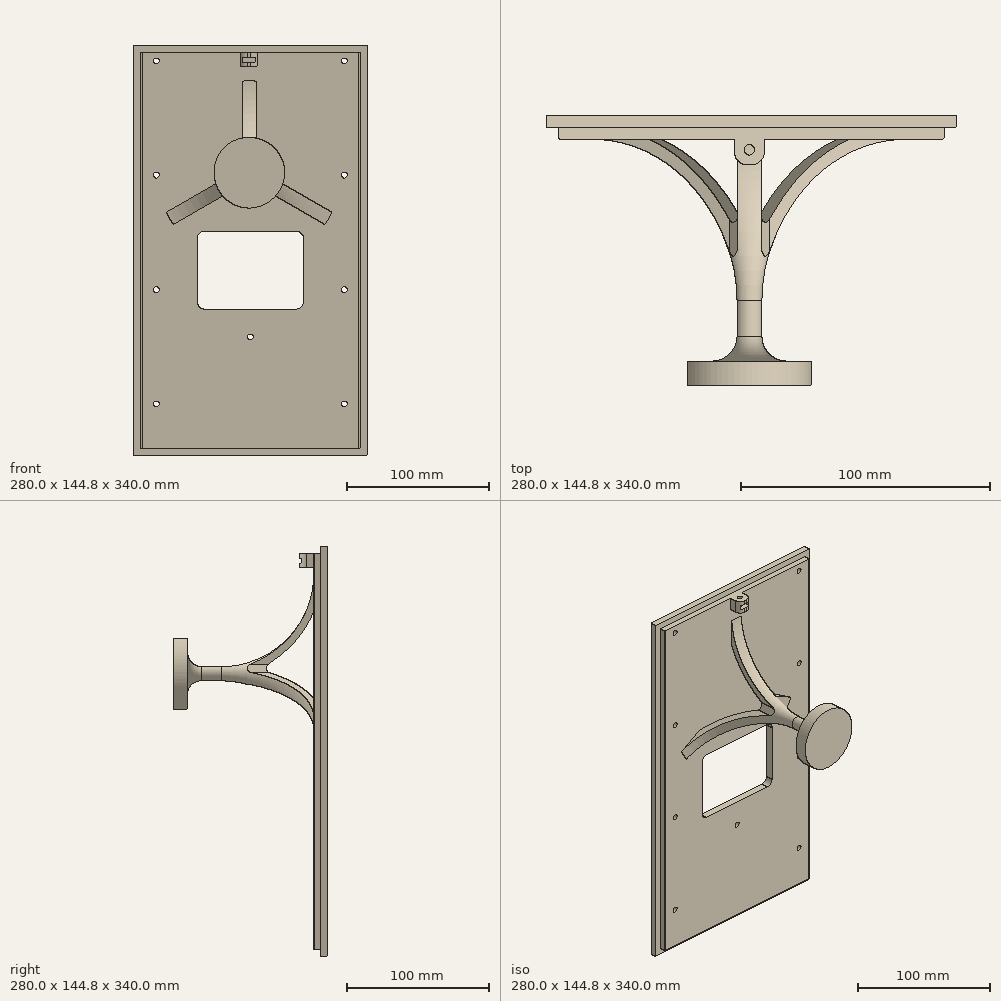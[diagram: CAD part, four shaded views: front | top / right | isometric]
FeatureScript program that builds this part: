
annotation { "Feature Type Name" : "Feature", "Feature Type Description" : "" }
export const myFeature = defineFeature(function(context is Context, id is Id, definition is map)
    precondition{}
    {
        {
            var Q0;
            Q0=qCreatedBy(makeId("Top.planeOp"),FACE);
            var sketch = newSketch(context, id + "F0", { "sketchPlane" : qUnion([Q0])});
            skLineSegment(sketch, "E0.bottom", {"start": v(-71.69, -76.13) * mm, "end": v(73.31, -76.13) * mm});
            skLineSegment(sketch, "E0.top", {"start": v(-71.69, 73.87) * mm, "end": v(73.31, 73.87) * mm});
            skLineSegment(sketch, "E0.left", {"start": v(-71.69, -76.13) * mm, "end": v(-71.69, 73.87) * mm});
            skLineSegment(sketch, "E0.right", {"start": v(73.31, -76.13) * mm, "end": v(73.31, 73.87) * mm});
            skPoint(sketch, "E0.middle", {"position": v(0.81, -1.13) * mm});
            skLineSegment(sketch, "E1.bottom", {"start": v(-81.69, -86.13) * mm, "end": v(83.31, -86.13) * mm});
            skLineSegment(sketch, "E1.top", {"start": v(-81.69, 83.87) * mm, "end": v(83.31, 83.87) * mm});
            skLineSegment(sketch, "E1.left", {"start": v(-81.69, -86.13) * mm, "end": v(-81.69, 83.87) * mm});
            skLineSegment(sketch, "E1.right", {"start": v(83.31, -86.13) * mm, "end": v(83.31, 83.87) * mm});
            skLineSegment(sketch, "E2", {"start": v(83.31, -81.13) * mm, "end": v(78.31, -81.13) * mm});
            skLineSegment(sketch, "E3", {"start": v(78.31, -81.13) * mm, "end": v(78.31, -76.13) * mm});
            skLineSegment(sketch, "E4", {"start": v(78.31, -76.13) * mm, "end": v(73.31, -76.13) * mm});
            skLineSegment(sketch, "E5", {"start": v(0.81, -86.13) * mm, "end": v(0.81, 83.87) * mm, "construction": true});
            skLineSegment(sketch, "E6", {"start": v(-81.69, -1.13) * mm, "end": v(83.31, -1.13) * mm, "construction": true});
            skLineSegment(sketch, "E7.MirrorCS", {"start": v(-76.69, -76.13) * mm, "end": v(-71.69, -76.13) * mm});
            skLineSegment(sketch, "E8.MirrorCS", {"start": v(-76.69, -81.13) * mm, "end": v(-76.69, -76.13) * mm});
            skLineSegment(sketch, "E9.MirrorCS", {"start": v(-81.69, -81.13) * mm, "end": v(-76.69, -81.13) * mm});
            skLineSegment(sketch, "E10.MirrorCS", {"start": v(83.31, 78.87) * mm, "end": v(78.31, 78.87) * mm});
            skLineSegment(sketch, "E11.MirrorCS", {"start": v(78.31, 78.87) * mm, "end": v(78.31, 73.87) * mm});
            skLineSegment(sketch, "E12.MirrorCS", {"start": v(78.31, 73.87) * mm, "end": v(73.31, 73.87) * mm});
            skLineSegment(sketch, "E13.MirrorCS", {"start": v(-76.69, 73.87) * mm, "end": v(-71.69, 73.87) * mm});
            skLineSegment(sketch, "E14.MirrorCS", {"start": v(-76.69, 78.87) * mm, "end": v(-76.69, 73.87) * mm});
            skLineSegment(sketch, "E15.MirrorCS", {"start": v(-81.69, 78.87) * mm, "end": v(-76.69, 78.87) * mm});
            skSolve(sketch);
        }
        {
            var Q0;
            Q0=makeQuery(id+"F0.imprint","IMPRINT",FACE,{"disambiguationData":[TD([[makeQuery(id+"F0.imprint","IMPRINT",EDGE,{"derivedFrom":sQuery(id+"F0.wireOp",EDGE,"E0.top")}),1.0]])]});
            extrude(context, id + "F1", {"entities" : qUnion([Q0]), "depth" : 290 * mm});
        }
        {
            var Q0;
            Q0=makeQuery(id+"F1.opExtrude","SWEPT_FACE",FACE,{"disambiguationData":[OSD([sQuery(id+"F0.wireOp",EDGE,"E11.MirrorCS")])]});
            var sketch = newSketch(context, id + "F2", { "sketchPlane" : qUnion([Q0])});
            skLineSegment(sketch, "E16.bottom", {"start": v(73.87, 290) * mm, "end": v(78.87, 290) * mm});
            skLineSegment(sketch, "E16.top", {"start": v(73.87, 285) * mm, "end": v(78.87, 285) * mm});
            skLineSegment(sketch, "E16.left", {"start": v(73.87, 290) * mm, "end": v(73.87, 285) * mm});
            skLineSegment(sketch, "E16.right", {"start": v(78.87, 290) * mm, "end": v(78.87, 285) * mm});
            skLineSegment(sketch, "E17.bottom", {"start": v(73.87, 0) * mm, "end": v(78.87, 0) * mm});
            skLineSegment(sketch, "E17.top", {"start": v(73.87, 5) * mm, "end": v(78.87, 5) * mm});
            skLineSegment(sketch, "E17.left", {"start": v(73.87, 0) * mm, "end": v(73.87, 5) * mm});
            skLineSegment(sketch, "E17.right", {"start": v(78.87, 0) * mm, "end": v(78.87, 5) * mm});
            skSolve(sketch);
        }
        {
            var Q0;
            Q0 = qSketchRegion(id + "F2", true);
            extrude(context, id + "F3", {"entities" : qUnion([Q0]), "operationType" : NewBodyOperationType.REMOVE, "endBound" : BoundingType.THROUGH_ALL, "oppositeDirection" : true, "depth" : 25 * mm});
        }
        {
            var Q0;
            Q0=makeQuery(id+"F1.opExtrude","SWEPT_FACE",FACE,{"disambiguationData":[OSD([sQuery(id+"F0.wireOp",EDGE,"E0.top"),sQuery(id+"F0.wireOp",EDGE,"E12.MirrorCS"),sQuery(id+"F0.wireOp",EDGE,"E13.MirrorCS")])]});
            var sketch = newSketch(context, id + "F4", { "sketchPlane" : qUnion([Q0])});
            skLineSegment(sketch, "E18", {"start": v(0, 290.68) * mm, "end": v(0, 0) * mm, "construction": true});
            skSolve(sketch);
        }
        {
            var Q0;
            Q0=sQuery(id+"F4.wireOp",EDGE,"A8UNbsVJ-gzvh-xwWj-zYQc-NNIxl5t48NZl");
            var Q1;
            Q1=sQuery(id+"F4.wireOp",EDGE,"E18");
            cPlane(context, id + "F5", {"entities" : qUnion([Q0, Q1]), "cplaneType" : CPlaneType.LINE_ANGLE, "offset" : 25 * mm, "angle" : 0 * degree, "width" : 150 * mm, "height" : 150 * mm});
        }
        {
            var Q0;
            Q0=qCreatedBy(id+"F5.planeOp",FACE);
            var sketch = newSketch(context, id + "F6", { "sketchPlane" : qUnion([Q0])});
            skLineSegment(sketch, "E19", {"start": v(15.13, 205) * mm, "end": v(15.13, 225) * mm});
            skLineSegment(sketch, "E20", {"start": v(15.13, 225) * mm, "end": v(25.13, 225) * mm});
            skLineSegment(sketch, "E21", {"start": v(25.13, 225) * mm, "end": v(25.13, 200) * mm});
            skLineSegment(sketch, "E22", {"start": v(25.13, 200) * mm, "end": v(-9.07, 200) * mm});
            skLineSegment(sketch, "E23", {"start": v(15.13, 205) * mm, "end": v(-9.07, 205) * mm});
            skPoint(sketch, "E24.visualSharp", {"position": v(-73.87, 205) * mm});
            skArc(sketch, "E24.filletArc", {"start": v(-73.87, 265) * mm, "mid": v(-53.22, 222.3) * mm, "end": v(-9.07, 205) * mm});
            skLineSegment(sketch, "E25", {"start": v(-73.87, 265) * mm, "end": v(-73.87, 243.54) * mm});
            skArc(sketch, "E26.0", {"start": v(-73.87, 243.54) * mm, "mid": v(-48.1, 211.9) * mm, "end": v(-9.07, 200) * mm});
            skSolve(sketch);
        }
        {
            var Q0;
            Q0=makeQuery(id+"F6.imprint","IMPRINT",FACE,{"disambiguationData":[TD([[makeQuery(id+"F6.imprint","IMPRINT",EDGE,{"derivedFrom":sQuery(id+"F6.wireOp",EDGE,"E19")}),-1.0]])]});
            var Q1;
            Q1=sQuery(id+"F6.wireOp",EDGE,"E22");
            revolve(context, id + "F7", {"operationType" : NewBodyOperationType.ADD, "entities" : qUnion([Q0]), "axis" : qUnion([Q1]), "revolveType" : RevolveType.FULL});
        }
        {
            var Q0;
            {var subQ0=sQuery(id+"F0.wireOp",EDGE,"E12.MirrorCS");var subQ1=sQuery(id+"F0.wireOp",EDGE,"E11.MirrorCS");Q0=makeQuery(id+"F4.imprint","IMPRINT",FACE,{"disambiguationData":[TD([[makeQuery(id+"F4.imprint","IMPRINT",EDGE,{"derivedFrom":makeQuery(id+"F1.opExtrude","SWEPT_EDGE",EDGE,{"disambiguationData":[OSD([subQ1,subQ0])]})}),-1.0]])]});}
            var sketch = newSketch(context, id + "F8", { "sketchPlane" : qUnion([Q0])});
            skLineSegment(sketch, "E27", {"start": v(0, 200) * mm, "end": v(0, 275.12) * mm, "construction": true});
            skLineSegment(sketch, "E28.left", {"start": v(5, 206.37) * mm, "end": v(5, 268.75) * mm});
            skLineSegment(sketch, "E28.right", {"start": v(-5, 206.37) * mm, "end": v(-5, 268.75) * mm});
            skPoint(sketch, "E28.middle", {"position": v(0, 237.56) * mm});
            skLineSegment(sketch, "E29.1.0", {"start": v(-8.02, 201.15) * mm, "end": v(-62.04, 169.95) * mm});
            skLineSegment(sketch, "E29.1.1", {"start": v(0, 200) * mm, "end": v(-65.06, 162.44) * mm, "construction": true});
            skLineSegment(sketch, "E29.1.2", {"start": v(-3.02, 192.49) * mm, "end": v(-57.04, 161.3) * mm});
            skLineSegment(sketch, "E29.2.0", {"start": v(3.02, 192.49) * mm, "end": v(57.04, 161.3) * mm});
            skLineSegment(sketch, "E29.2.1", {"start": v(0, 200) * mm, "end": v(65.06, 162.44) * mm, "construction": true});
            skLineSegment(sketch, "E29.2.2", {"start": v(8.02, 201.15) * mm, "end": v(62.04, 169.95) * mm});
            skPoint(sketch, "E29.center", {"position": v(0, 200) * mm});
            skArc(sketch, "E30", {"start": v(-57.04, 161.3) * mm, "mid": v(0, 131.07) * mm, "end": v(57.04, 161.3) * mm});
            skArc(sketch, "E31.trimOffspring", {"start": v(62.04, 169.95) * mm, "mid": v(59.7, 234.47) * mm, "end": v(5, 268.75) * mm});
            skArc(sketch, "E32.trimOffspring", {"start": v(-5, 268.75) * mm, "mid": v(-59.7, 234.47) * mm, "end": v(-62.04, 169.95) * mm});
            skLineSegment(sketch, "E33", {"start": v(-5, 206.37) * mm, "end": v(-8.02, 201.15) * mm});
            skLineSegment(sketch, "E34", {"start": v(-3.02, 192.49) * mm, "end": v(3.02, 192.49) * mm});
            skLineSegment(sketch, "E35", {"start": v(8.02, 201.15) * mm, "end": v(5, 206.37) * mm});
            skSolve(sketch);
        }
        {
            var Q0;
            Q0 = qSketchRegion(id + "F8", true);
            var Q1;
            Q1=makeQuery(id+"F7.opRevolve","SWEPT_FACE",FACE,{"disambiguationData":[OSD([sQuery(id+"F6.wireOp",EDGE,"E19")])]});
            extrude(context, id + "F9", {"entities" : qUnion([Q0]), "operationType" : NewBodyOperationType.REMOVE, "endBound" : BoundingType.UP_TO_SURFACE, "endBoundEntityFace" : qUnion([Q1]), "depth" : 25 * mm});
        }
        {
            var Q0;
            Q0=makeQuery(id+"F1.opExtrude","SWEPT_FACE",FACE,{"disambiguationData":[OSD([sQuery(id+"F0.wireOp",EDGE,"E1.top")])]});
            var sketch = newSketch(context, id + "F10", { "sketchPlane" : qUnion([Q0])});
            skPoint(sketch, "E36", {"position": v(-67.31, 279) * mm});
            skPoint(sketch, "E37.0.1.0", {"position": v(-67.31, 198.17) * mm});
            skPoint(sketch, "E37.0.2.0", {"position": v(-67.31, 117.33) * mm});
            skPoint(sketch, "E37.0.3.0", {"position": v(-67.31, 36.5) * mm});
            skLineSegment(sketch, "E37.direction1", {"start": v(-67.31, 279) * mm, "end": v(-42.31, 279) * mm, "construction": true});
            skLineSegment(sketch, "E37.direction2", {"start": v(-67.31, 279) * mm, "end": v(-67.31, 198.17) * mm, "construction": true});
            skPoint(sketch, "E38", {"position": v(65.69, 279) * mm});
            skPoint(sketch, "E39", {"position": v(65.69, 198.17) * mm});
            skPoint(sketch, "E40", {"position": v(65.69, 117.33) * mm});
            skPoint(sketch, "E41", {"position": v(65.69, 36.5) * mm});
            skPoint(sketch, "E42", {"position": v(-0.81, 83.9) * mm});
            skLineSegment(sketch, "E43", {"start": v(-0.81, 83.9) * mm, "end": v(81.69, 83.9) * mm, "construction": true});
            skLineSegment(sketch, "E44", {"start": v(-0.81, 83.9) * mm, "end": v(-83.31, 83.9) * mm, "construction": true});
            skSolve(sketch);
        }
        {
            var Q0;
            Q0=sQuery(id+"F10.wireOp",VERTEX,"E36");
            var Q1;
            Q1=sQuery(id+"F10.wireOp",VERTEX,"E37.0.1.0");
            var Q2;
            Q2=sQuery(id+"F10.wireOp",VERTEX,"E37.0.2.0");
            var Q3;
            Q3=sQuery(id+"F10.wireOp",VERTEX,"E37.0.3.0");
            var Q4;
            Q4=sQuery(id+"F10.wireOp",VERTEX,"9bec949c-2aa9-4da3-a5e8-29f5872e4faf5.MirrorP");
            var Q5;
            Q5=sQuery(id+"F10.wireOp",VERTEX,"9bec949c-2aa9-4da3-a5e8-29f5872e4faf4.MirrorP");
            var Q6;
            Q6=sQuery(id+"F10.wireOp",VERTEX,"9bec949c-2aa9-4da3-a5e8-29f5872e4faf1.MirrorP");
            var Q7;
            Q7=sQuery(id+"F10.wireOp",VERTEX,"9bec949c-2aa9-4da3-a5e8-29f5872e4faf0.MirrorP");
            var Q8;
            Q8=sQuery(id+"F10.wireOp",VERTEX,"552721cf-935c-4b78-bc10-7440b418902f1.MirrorP");
            var Q9;
            Q9=sQuery(id+"F10.wireOp",VERTEX,"552721cf-935c-4b78-bc10-7440b418902f3.MirrorP");
            var Q10;
            Q10=sQuery(id+"F10.wireOp",VERTEX,"552721cf-935c-4b78-bc10-7440b418902f2.MirrorP");
            var Q11;
            Q11=sQuery(id+"F10.wireOp",VERTEX,"552721cf-935c-4b78-bc10-7440b418902f0.MirrorP");
            var Q12;
            Q12=sQuery(id+"F10.wireOp",VERTEX,"E38");
            var Q13;
            Q13=sQuery(id+"F10.wireOp",VERTEX,"E39");
            var Q14;
            Q14=sQuery(id+"F10.wireOp",VERTEX,"E40");
            var Q15;
            Q15=sQuery(id+"F10.wireOp",VERTEX,"E41");
            var Q16;
            Q16=sQuery(id+"F10.wireOp",VERTEX,"E42");
            var Q17;
            Q17=sQuery(id+"F10.wireOp",VERTEX,"88696ca7-52d1-4865-b397-7ea25439fa9f");
            var Q18;
            Q18=makeQuery(id+"F1.opExtrude","SWEPT_BODY",BODY,{"disambiguationData":[OSD([sQuery(id+"F0.wireOp",EDGE,"E0.top"),sQuery(id+"F0.wireOp",EDGE,"E1.top"),sQuery(id+"F0.wireOp",EDGE,"E1.left"),sQuery(id+"F0.wireOp",EDGE,"E1.right"),sQuery(id+"F0.wireOp",EDGE,"E10.MirrorCS"),sQuery(id+"F0.wireOp",EDGE,"E11.MirrorCS"),sQuery(id+"F0.wireOp",EDGE,"E12.MirrorCS"),sQuery(id+"F0.wireOp",EDGE,"E13.MirrorCS"),sQuery(id+"F0.wireOp",EDGE,"E14.MirrorCS"),sQuery(id+"F0.wireOp",EDGE,"E15.MirrorCS")])]});
            hole(context, id + "F11", {"style" : HoleStyle.C_SINK, "endStyle" : HoleEndStyle.THROUGH, "holeDiameter" : 4.12 * mm, "cSinkDiameter" : 9.12 * mm, "cSinkAngle" : 82 * degree, "locations" : qUnion([Q0, Q1, Q2, Q3, Q4, Q5, Q6, Q7, Q8, Q9, Q10, Q11, Q12, Q13, Q14, Q15, Q16, Q17]), "scope" : qUnion([Q18]), "isTappedThrough" : true});
        }
        {
            var Q0;
            {var subQ0=sQuery(id+"F0.wireOp",EDGE,"E12.MirrorCS");var subQ1=sQuery(id+"F0.wireOp",EDGE,"E11.MirrorCS");Q0=makeQuery(id+"F4.imprint","IMPRINT",FACE,{"disambiguationData":[TD([[makeQuery(id+"F4.imprint","IMPRINT",EDGE,{"derivedFrom":makeQuery(id+"F1.opExtrude","SWEPT_EDGE",EDGE,{"disambiguationData":[OSD([subQ1,subQ0])]})}),-1.0]])]});}
            var sketch = newSketch(context, id + "F12", { "sketchPlane" : qUnion([Q0])});
            skLineSegment(sketch, "E45.bottom", {"start": v(38.31, 103.5) * mm, "end": v(-36.69, 103.5) * mm});
            skLineSegment(sketch, "E45.top", {"start": v(38.31, 158.5) * mm, "end": v(-36.69, 158.5) * mm});
            skLineSegment(sketch, "E45.left", {"start": v(38.31, 103.5) * mm, "end": v(38.31, 158.5) * mm});
            skLineSegment(sketch, "E45.right", {"start": v(-36.69, 103.5) * mm, "end": v(-36.69, 158.5) * mm});
            skPoint(sketch, "E45.middle", {"position": v(0.81, 131) * mm});
            skLineSegment(sketch, "E46", {"start": v(38.31, 131) * mm, "end": v(83.31, 131) * mm, "construction": true});
            skPoint(sketch, "E46.endSnap0", {"position": v(38.31, 131) * mm});
            skLineSegment(sketch, "E47", {"start": v(-36.69, 131) * mm, "end": v(-81.69, 131) * mm, "construction": true});
            skSolve(sketch);
        }
        {
            var Q0;
            Q0 = qSketchRegion(id + "F12", true);
            extrude(context, id + "F13", {"entities" : qUnion([Q0]), "operationType" : NewBodyOperationType.REMOVE, "endBound" : BoundingType.THROUGH_ALL, "oppositeDirection" : true, "depth" : 25 * mm});
        }
        {
            var Q0;
            Q0=makeQuery(id+"F1.opExtrude","SWEPT_FACE",FACE,{"disambiguationData":[OSD([sQuery(id+"F0.wireOp",EDGE,"E1.top")])]});
            var sketch = newSketch(context, id + "F14", { "sketchPlane" : qUnion([Q0])});
            skLineSegment(sketch, "E48.bottom", {"start": v(46.19, 91) * mm, "end": v(-47.81, 91) * mm});
            skLineSegment(sketch, "E48.top", {"start": v(46.19, 171) * mm, "end": v(-47.81, 171) * mm});
            skLineSegment(sketch, "E48.left", {"start": v(46.19, 91) * mm, "end": v(46.19, 171) * mm});
            skLineSegment(sketch, "E48.right", {"start": v(-47.81, 91) * mm, "end": v(-47.81, 171) * mm});
            skPoint(sketch, "E48.middle.positionSnap0", {"position": v(36.69, 131) * mm});
            skPoint(sketch, "E48.centerSnap0", {"position": v(36.69, 131) * mm});
            skLineSegment(sketch, "E49", {"start": v(-47.81, 131) * mm, "end": v(-83.31, 131) * mm, "construction": true});
            skLineSegment(sketch, "E50", {"start": v(46.19, 131) * mm, "end": v(81.69, 131) * mm, "construction": true});
            skSolve(sketch);
        }
        {
            var Q0;
            Q0 = qSketchRegion(id + "F14", true);
            extrude(context, id + "F15", {"entities" : qUnion([Q0]), "operationType" : NewBodyOperationType.REMOVE, "oppositeDirection" : true, "depth" : 4 * mm});
        }
        {
            var Q0;
            Q0=makeQuery(id+"F3.boolean.opBoolean","COPY",FACE,{"derivedFrom":makeQuery(id+"F3.opExtrude","SWEPT_FACE",FACE,{"disambiguationData":[OSD([sQuery(id+"F2.wireOp",EDGE,"E16.top")])]})});
            var sketch = newSketch(context, id + "F16", { "sketchPlane" : qUnion([Q0])});
            skLineSegment(sketch, "E51.bottom", {"start": v(6, 73.87) * mm, "end": v(-6, 73.87) * mm});
            skLineSegment(sketch, "E51.top", {"start": v(1, 63.87) * mm, "end": v(-1, 63.87) * mm});
            skLineSegment(sketch, "E51.left", {"start": v(6, 73.87) * mm, "end": v(6, 68.87) * mm});
            skLineSegment(sketch, "E51.right", {"start": v(-6, 73.87) * mm, "end": v(-6, 68.87) * mm});
            skPoint(sketch, "E51.middle", {"position": v(0, 68.87) * mm});
            skPoint(sketch, "E52.visualSharp", {"position": v(6, 63.87) * mm});
            skArc(sketch, "E52.filletArc", {"start": v(1, 63.87) * mm, "mid": v(4.54, 65.34) * mm, "end": v(6, 68.87) * mm});
            skPoint(sketch, "E53.visualSharp", {"position": v(-6, 63.87) * mm});
            skArc(sketch, "E53.filletArc", {"start": v(-6, 68.87) * mm, "mid": v(-4.54, 65.34) * mm, "end": v(-1, 63.87) * mm});
            skCircle(sketch, "E54", {"center": v(0, 69.87) * mm, "radius": 2.08 * mm});
            skPoint(sketch, "E54.centerSnap0", {"position": v(0, 73.87) * mm});
            skSolve(sketch);
        }
        {
            var Q0;
            Q0=makeQuery(id+"F16.imprint","IMPRINT",FACE,{"disambiguationData":[TD([[makeQuery(id+"F16.imprint","IMPRINT",EDGE,{"derivedFrom":sQuery(id+"F16.wireOp",EDGE,"E51.bottom")}),-1.0]])]});
            extrude(context, id + "F17", {"entities" : qUnion([Q0]), "operationType" : NewBodyOperationType.ADD, "oppositeDirection" : true, "depth" : 10 * mm});
        }
        {
            var Q0;
            Q0=makeQuery(id+"F17.opExtrude","SWEPT_FACE",FACE,{"disambiguationData":[OSD([sQuery(id+"F16.wireOp",EDGE,"E51.top")])]});
            var sketch = newSketch(context, id + "F18", { "sketchPlane" : qUnion([Q0])});
            skLineSegment(sketch, "E55.bottom", {"start": v(4.5, 278.25) * mm, "end": v(-4.5, 278.25) * mm});
            skLineSegment(sketch, "E55.top", {"start": v(4.5, 281.75) * mm, "end": v(-4.5, 281.75) * mm});
            skLineSegment(sketch, "E55.left", {"start": v(4.5, 278.25) * mm, "end": v(4.5, 281.75) * mm});
            skLineSegment(sketch, "E55.right", {"start": v(-4.5, 278.25) * mm, "end": v(-4.5, 281.75) * mm});
            skPoint(sketch, "E55.middle", {"position": v(0, 280) * mm});
            skPoint(sketch, "E55.middle.positionSnap0", {"position": v(0, 285) * mm});
            skPoint(sketch, "E55.middle.positionSnap1", {"position": v(-1, 280) * mm});
            skPoint(sketch, "E55.centerSnap0", {"position": v(0, 285) * mm});
            skPoint(sketch, "E55.centerSnap1", {"position": v(-1, 280) * mm});
            skSolve(sketch);
        }
        {
            var Q0;
            Q0 = qSketchRegion(id + "F18", true);
            extrude(context, id + "F19", {"entities" : qUnion([Q0]), "operationType" : NewBodyOperationType.REMOVE, "oppositeDirection" : true, "depth" : 11.25 * mm});
        }
        {
            var Q0;
            Q0=makeQuery(id+"F3.boolean.opBoolean","COPY",EDGE,{"derivedFrom":makeQuery(id+"F3.opExtrude","SWEPT_EDGE",EDGE,{"disambiguationData":[OSD([sQuery(id+"F0.wireOp",EDGE,"E11.MirrorCS"),sQuery(id+"F0.wireOp",EDGE,"E12.MirrorCS"),sQuery(id+"F2.wireOp",EDGE,"E16.top"),sQuery(id+"F2.wireOp",EDGE,"E16.left")])]})});
            var Q1;
            Q1=makeQuery(id+"F1.opExtrude","SWEPT_EDGE",EDGE,{"disambiguationData":[OSD([sQuery(id+"F0.wireOp",EDGE,"E13.MirrorCS"),sQuery(id+"F0.wireOp",EDGE,"E14.MirrorCS")])]});
            var Q2;
            Q2=makeQuery(id+"F3.boolean.opBoolean","COPY",EDGE,{"derivedFrom":makeQuery(id+"F3.opExtrude","SWEPT_EDGE",EDGE,{"disambiguationData":[OSD([sQuery(id+"F0.wireOp",EDGE,"E11.MirrorCS"),sQuery(id+"F0.wireOp",EDGE,"E12.MirrorCS"),sQuery(id+"F2.wireOp",EDGE,"E17.top"),sQuery(id+"F2.wireOp",EDGE,"E17.left")])]})});
            var Q3;
            Q3=makeQuery(id+"F1.opExtrude","SWEPT_EDGE",EDGE,{"disambiguationData":[OSD([sQuery(id+"F0.wireOp",EDGE,"E11.MirrorCS"),sQuery(id+"F0.wireOp",EDGE,"E12.MirrorCS")])]});
            fillet(context, id + "F20", {"entities" : qUnion([Q0, Q1, Q2, Q3]), "radius" : 1 * mm, "tangentPropagation" : true, "allowEdgeOverflow" : false});
        }
        {
            var Q0;
            Q0=makeQuery(id+"F7.opRevolve","SWEPT_EDGE",EDGE,{"disambiguationData":[OSD([sQuery(id+"F6.wireOp",EDGE,"E19"),sQuery(id+"F6.wireOp",EDGE,"E23")])]});
            fillet(context, id + "F21", {"entities" : qUnion([Q0]), "radius" : 10 * mm, "tangentPropagation" : true, "allowEdgeOverflow" : false});
        }
        {
            var Q0;
            Q0=makeQuery(id+"F15.boolean.opBoolean","COPY",EDGE,{"derivedFrom":makeQuery(id+"F15.opExtrude","SWEPT_EDGE",EDGE,{"disambiguationData":[OSD([sQuery(id+"F14.wireOp",EDGE,"E48.bottom"),sQuery(id+"F14.wireOp",EDGE,"E48.right")])]})});
            var Q1;
            Q1=makeQuery(id+"F13.boolean.opBoolean","COPY",EDGE,{"derivedFrom":makeQuery(id+"F13.opExtrude","SWEPT_EDGE",EDGE,{"disambiguationData":[OSD([sQuery(id+"F12.wireOp",EDGE,"E45.bottom"),sQuery(id+"F12.wireOp",EDGE,"E45.left")])]})});
            var Q2;
            Q2=makeQuery(id+"F13.boolean.opBoolean","COPY",EDGE,{"derivedFrom":makeQuery(id+"F13.opExtrude","SWEPT_EDGE",EDGE,{"disambiguationData":[OSD([sQuery(id+"F12.wireOp",EDGE,"E45.bottom"),sQuery(id+"F12.wireOp",EDGE,"E45.right")])]})});
            var Q3;
            Q3=makeQuery(id+"F15.boolean.opBoolean","COPY",EDGE,{"derivedFrom":makeQuery(id+"F15.opExtrude","SWEPT_EDGE",EDGE,{"disambiguationData":[OSD([sQuery(id+"F14.wireOp",EDGE,"E48.bottom"),sQuery(id+"F14.wireOp",EDGE,"E48.left")])]})});
            var Q4;
            Q4=makeQuery(id+"F13.boolean.opBoolean","COPY",EDGE,{"derivedFrom":makeQuery(id+"F13.opExtrude","SWEPT_EDGE",EDGE,{"disambiguationData":[OSD([sQuery(id+"F12.wireOp",EDGE,"E45.top"),sQuery(id+"F12.wireOp",EDGE,"E45.right")])]})});
            var Q5;
            Q5=makeQuery(id+"F15.boolean.opBoolean","COPY",EDGE,{"derivedFrom":makeQuery(id+"F15.opExtrude","SWEPT_EDGE",EDGE,{"disambiguationData":[OSD([sQuery(id+"F14.wireOp",EDGE,"E48.top"),sQuery(id+"F14.wireOp",EDGE,"E48.left")])]})});
            var Q6;
            Q6=makeQuery(id+"F15.boolean.opBoolean","COPY",EDGE,{"derivedFrom":makeQuery(id+"F15.opExtrude","SWEPT_EDGE",EDGE,{"disambiguationData":[OSD([sQuery(id+"F14.wireOp",EDGE,"E48.top"),sQuery(id+"F14.wireOp",EDGE,"E48.right")])]})});
            var Q7;
            Q7=makeQuery(id+"F13.boolean.opBoolean","COPY",EDGE,{"derivedFrom":makeQuery(id+"F13.opExtrude","SWEPT_EDGE",EDGE,{"disambiguationData":[OSD([sQuery(id+"F12.wireOp",EDGE,"E45.top"),sQuery(id+"F12.wireOp",EDGE,"E45.left")])]})});
            fillet(context, id + "F22", {"entities" : qUnion([Q0, Q1, Q2, Q3, Q4, Q5, Q6, Q7]), "radius" : 5 * mm, "tangentPropagation" : true, "allowEdgeOverflow" : false});
        }
    });
